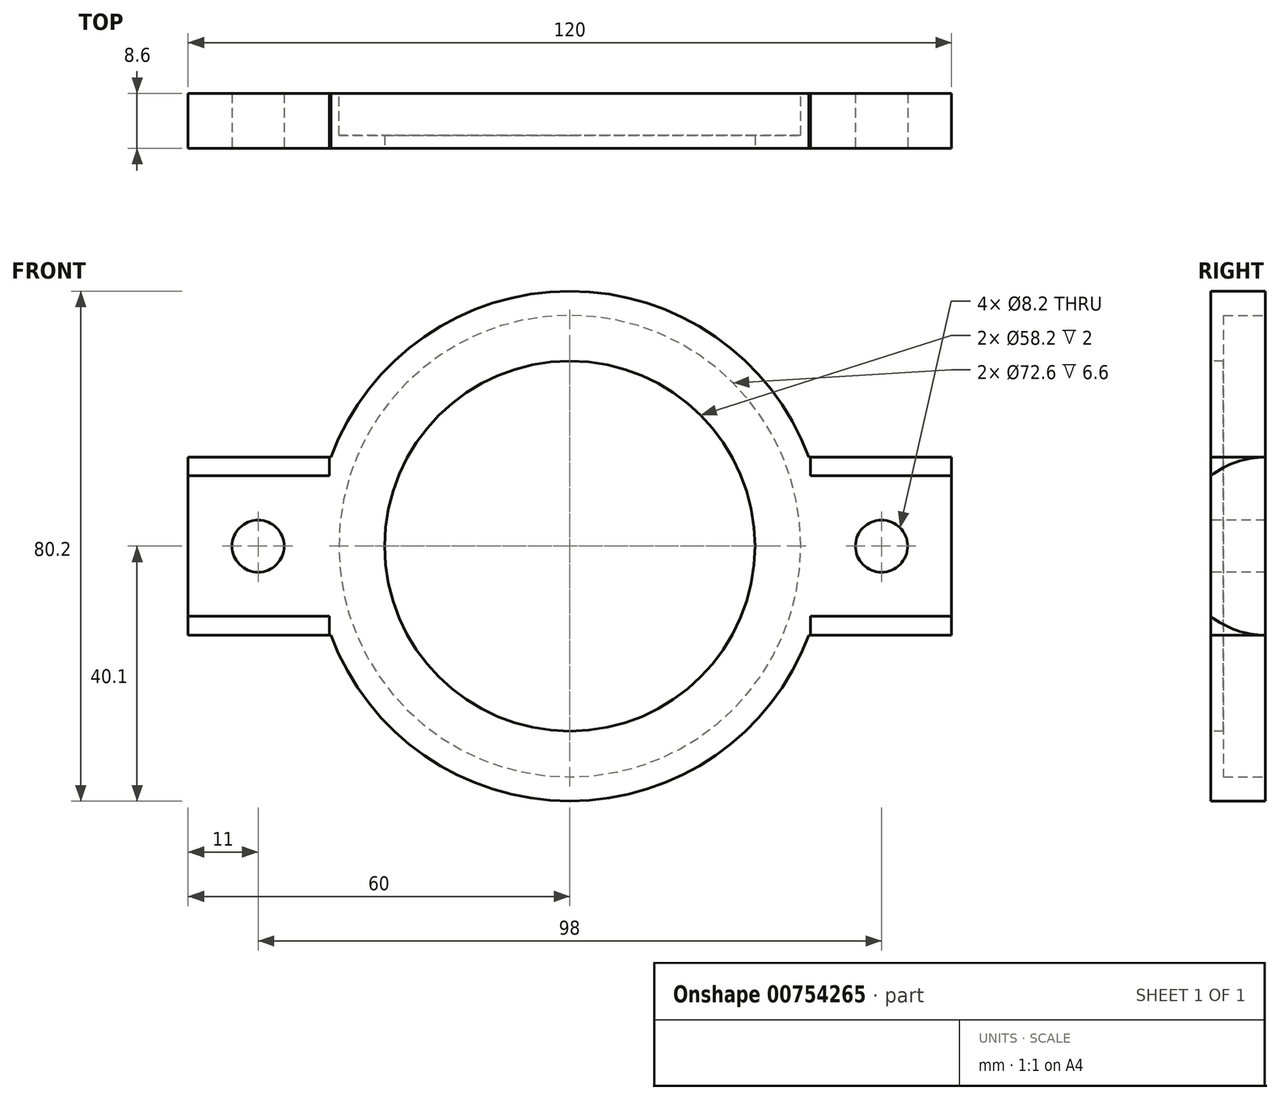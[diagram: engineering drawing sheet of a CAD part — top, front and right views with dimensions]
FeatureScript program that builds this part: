
annotation { "Feature Type Name" : "Feature", "Feature Type Description" : "" }
export const myFeature = defineFeature(function(context is Context, id is Id, definition is map)
    precondition{}
    {
        {
            var Q0;
            Q0=qCreatedBy(makeId("Front.planeOp"),FACE);
            var sketch = newSketch(context, id + "F0", { "sketchPlane" : qUnion([Q0])});
            skLineSegment(sketch, "E0.bottom", {"start": v(-60, 14) * mm, "end": v(60, 14) * mm});
            skLineSegment(sketch, "E0.top", {"start": v(-60, -14) * mm, "end": v(60, -14) * mm});
            skLineSegment(sketch, "E0.left", {"start": v(-60, 14) * mm, "end": v(-60, -14) * mm});
            skLineSegment(sketch, "E0.right", {"start": v(60, 14) * mm, "end": v(60, -14) * mm});
            skPoint(sketch, "E0.middle", {"position": v(0, 0) * mm});
            skSolve(sketch);
        }
        {
            var Q0;
            Q0=makeQuery(id+"F0.imprint","IMPRINT",FACE,{"disambiguationData":[TD([[makeQuery(id+"F0.imprint","IMPRINT",EDGE,{"derivedFrom":sQuery(id+"F0.wireOp",EDGE,"E0.bottom")}),-1.0]])]});
            extrude(context, id + "F1", {"entities" : qUnion([Q0]), "depth" : 8.6 * mm, "offsetDistance" : 25 * mm});
        }
        {
            var Q0;
            Q0=makeQuery(id+"F1.opExtrude","CAP_FACE",FACE,{"disambiguationData":[OSD([sQuery(id+"F0.wireOp",EDGE,"E0.bottom"),sQuery(id+"F0.wireOp",EDGE,"E0.top"),sQuery(id+"F0.wireOp",EDGE,"E0.left"),sQuery(id+"F0.wireOp",EDGE,"E0.right")])],"isStart":false});
            var sketch = newSketch(context, id + "F2", { "sketchPlane" : qUnion([Q0])});
            skCircle(sketch, "E1", {"center": v(0, 0) * mm, "radius": 40.1 * mm});
            skCircle(sketch, "E2", {"center": v(0, 0) * mm, "radius": 29.1 * mm});
            skSolve(sketch);
        }
        {
            var Q0;
            {var subQ0=sQuery(id+"F2.wireOp",EDGE,"E2");var subQ1=makeQuery(id+"F1.opExtrude","CAP_EDGE",EDGE,{"disambiguationData":[OSD([sQuery(id+"F0.wireOp",EDGE,"E0.bottom")])],"isStart":false});var subQ2=makeQuery(id+"F2.imprint","INTERSECT",VERTEX,{"disambiguationData":[OD(0.0)],"derivedFrom":[subQ1,subQ0]});Q0=makeQuery(id+"F2.imprint","IMPRINT",FACE,{"disambiguationData":[TD([[makeQuery(id+"F2.imprint","IMPRINT",EDGE,{"disambiguationData":[TD([[subQ2,1.0]])],"derivedFrom":subQ0}),1.0]])]});}
            var Q1;
            {var subQ0=sQuery(id+"F2.wireOp",EDGE,"E2");var subQ1=makeQuery(id+"F1.opExtrude","CAP_EDGE",EDGE,{"disambiguationData":[OSD([sQuery(id+"F0.wireOp",EDGE,"E0.bottom")])],"isStart":false});var subQ2=makeQuery(id+"F2.imprint","INTERSECT",VERTEX,{"disambiguationData":[OD(0.0)],"derivedFrom":[subQ1,subQ0]});Q1=makeQuery(id+"F2.imprint","IMPRINT",FACE,{"disambiguationData":[TD([[makeQuery(id+"F2.imprint","IMPRINT",EDGE,{"disambiguationData":[TD([[subQ2,-1.0]])],"derivedFrom":subQ0}),1.0]])]});}
            var Q2;
            {var subQ0=sQuery(id+"F2.wireOp",EDGE,"E2");var subQ1=makeQuery(id+"F1.opExtrude","CAP_EDGE",EDGE,{"disambiguationData":[OSD([sQuery(id+"F0.wireOp",EDGE,"E0.top")])],"isStart":false});var subQ2=makeQuery(id+"F2.imprint","INTERSECT",VERTEX,{"disambiguationData":[OD(0.0)],"derivedFrom":[subQ1,subQ0]});Q2=makeQuery(id+"F2.imprint","IMPRINT",FACE,{"disambiguationData":[TD([[makeQuery(id+"F2.imprint","IMPRINT",EDGE,{"disambiguationData":[TD([[subQ2,-1.0]])],"derivedFrom":subQ0}),1.0]])]});}
            extrude(context, id + "F3", {"entities" : qUnion([Q0, Q1, Q2]), "operationType" : NewBodyOperationType.REMOVE, "endBound" : BoundingType.THROUGH_ALL, "oppositeDirection" : true, "depth" : 25 * mm, "offsetDistance" : 25 * mm});
        }
        {
            var Q0;
            Q0 = qSketchRegion(id + "F2", true);
            extrude(context, id + "F4", {"entities" : qUnion([Q0]), "oppositeDirection" : true, "depth" : 8.6 * mm, "offsetDistance" : 25 * mm});
        }
        {
            var Q0;
            Q0=makeQuery(id+"F3.boolean.opBoolean","SPLIT",BODY,{"disambiguationData":[OD(0.0)],"derivedFrom":makeQuery(id+"F1.opExtrude","SWEPT_BODY",BODY,{"disambiguationData":[OSD([sQuery(id+"F0.wireOp",EDGE,"E0.bottom"),sQuery(id+"F0.wireOp",EDGE,"E0.top"),sQuery(id+"F0.wireOp",EDGE,"E0.left"),sQuery(id+"F0.wireOp",EDGE,"E0.right")])]})});
            var Q1;
            Q1=makeQuery(id+"F3.boolean.opBoolean","SPLIT",BODY,{"disambiguationData":[OD(1.0)],"derivedFrom":makeQuery(id+"F1.opExtrude","SWEPT_BODY",BODY,{"disambiguationData":[OSD([sQuery(id+"F0.wireOp",EDGE,"E0.bottom"),sQuery(id+"F0.wireOp",EDGE,"E0.top"),sQuery(id+"F0.wireOp",EDGE,"E0.left"),sQuery(id+"F0.wireOp",EDGE,"E0.right")])]})});
            var Q2;
            Q2=makeQuery(id+"F4.opExtrude","SWEPT_BODY",BODY,{"disambiguationData":[OSD([sQuery(id+"F2.wireOp",EDGE,"E1"),sQuery(id+"F2.wireOp",EDGE,"E2")])]});
            booleanBodies(context, id + "F5", {"operationType" : BooleanOperationType.UNION, "tools" : qUnion([Q0, Q1, Q2])});
        }
        {
            var Q0;
            {var subQ0=sQuery(id+"F2.wireOp",EDGE,"E2");var subQ1=sQuery(id+"F0.wireOp",EDGE,"E0.bottom");var subQ3=sQuery(id+"F0.wireOp",EDGE,"E0.right");var subQ4=sQuery(id+"F0.wireOp",EDGE,"E0.top");var subQ7=sQuery(id+"F0.wireOp",EDGE,"E0.left");var subQ8=makeQuery(id+"F1.opExtrude","CAP_FACE",FACE,{"disambiguationData":[OSD([subQ1,subQ4,subQ7,subQ3])],"isStart":false});Q0=makeQuery(id+"F5.opBoolean","MERGE",FACE,{"derivedFrom":[makeQuery(id+"F3.boolean.opBoolean","SPLIT",FACE,{"disambiguationData":[TD([makeQuery(id+"F1.opExtrude","SWEPT_FACE",FACE,{"disambiguationData":[OSD([subQ7])]})])],"derivedFrom":subQ8}),makeQuery(id+"F3.boolean.opBoolean","SPLIT",FACE,{"disambiguationData":[TD([makeQuery(id+"F1.opExtrude","SWEPT_FACE",FACE,{"disambiguationData":[OSD([subQ3])]})])],"derivedFrom":subQ8}),makeQuery(id+"F4.opExtrude","CAP_FACE",FACE,{"disambiguationData":[OSD([sQuery(id+"F2.wireOp",EDGE,"E1"),subQ0])],"isStart":true})]});}
            var sketch = newSketch(context, id + "F6", { "sketchPlane" : qUnion([Q0])});
            skCircle(sketch, "E3", {"center": v(-49, 0) * mm, "radius": 4.1 * mm});
            skCircle(sketch, "E4", {"center": v(49, 0) * mm, "radius": 4.1 * mm});
            skSolve(sketch);
        }
        {
            var Q0;
            Q0=makeQuery(id+"F6.imprint","IMPRINT",FACE,{"disambiguationData":[TD([[makeQuery(id+"F6.imprint","IMPRINT",EDGE,{"derivedFrom":sQuery(id+"F6.wireOp",EDGE,"E3")}),1.0]])]});
            var Q1;
            Q1=makeQuery(id+"F6.imprint","IMPRINT",FACE,{"disambiguationData":[TD([[makeQuery(id+"F6.imprint","IMPRINT",EDGE,{"derivedFrom":sQuery(id+"F6.wireOp",EDGE,"E4")}),1.0]])]});
            extrude(context, id + "F7", {"entities" : qUnion([Q0, Q1]), "operationType" : NewBodyOperationType.REMOVE, "endBound" : BoundingType.THROUGH_ALL, "oppositeDirection" : true, "depth" : 25 * mm, "offsetDistance" : 25 * mm});
        }
        {
            var Q0;
            Q0=makeQuery(id+"F1.opExtrude","SWEPT_FACE",FACE,{"disambiguationData":[OSD([sQuery(id+"F0.wireOp",EDGE,"E0.right")])]});
            var sketch = newSketch(context, id + "F8", { "sketchPlane" : qUnion([Q0])});
            skCircle(sketch, "E5", {"center": v(0, 0) * mm, "radius": 14 * mm});
            skSolve(sketch);
        }
        {
            var Q0;
            {var subQ1=sQuery(id+"F0.wireOp",EDGE,"E0.right");var subQ2=makeQuery(id+"F1.opExtrude","SWEPT_EDGE",EDGE,{"disambiguationData":[OSD([sQuery(id+"F0.wireOp",EDGE,"E0.bottom"),subQ1])]});Q0=makeQuery(id+"F8.imprint","IMPRINT",FACE,{"disambiguationData":[TD([[makeQuery(id+"F8.imprint","IMPRINT",EDGE,{"derivedFrom":subQ2}),-1.0]])]});}
            var Q1;
            {var subQ1=sQuery(id+"F0.wireOp",EDGE,"E0.right");var subQ2=makeQuery(id+"F1.opExtrude","SWEPT_EDGE",EDGE,{"disambiguationData":[OSD([sQuery(id+"F0.wireOp",EDGE,"E0.top"),subQ1])]});Q1=makeQuery(id+"F8.imprint","IMPRINT",FACE,{"disambiguationData":[TD([[makeQuery(id+"F8.imprint","IMPRINT",EDGE,{"derivedFrom":subQ2}),1.0]])]});}
            extrude(context, id + "F9", {"entities" : qUnion([Q0, Q1]), "operationType" : NewBodyOperationType.REMOVE, "oppositeDirection" : true, "depth" : 22.2 * mm, "offsetDistance" : 25 * mm});
        }
        {
            var Q0;
            Q0=makeQuery(id+"F1.opExtrude","SWEPT_FACE",FACE,{"disambiguationData":[OSD([sQuery(id+"F0.wireOp",EDGE,"E0.left")])]});
            var sketch = newSketch(context, id + "F10", { "sketchPlane" : qUnion([Q0])});
            skCircle(sketch, "E6", {"center": v(0, 0) * mm, "radius": 14 * mm});
            skSolve(sketch);
        }
        {
            var Q0;
            {var subQ1=sQuery(id+"F0.wireOp",EDGE,"E0.left");var subQ2=makeQuery(id+"F1.opExtrude","SWEPT_EDGE",EDGE,{"disambiguationData":[OSD([sQuery(id+"F0.wireOp",EDGE,"E0.bottom"),subQ1])]});Q0=makeQuery(id+"F10.imprint","IMPRINT",FACE,{"disambiguationData":[TD([[makeQuery(id+"F10.imprint","IMPRINT",EDGE,{"derivedFrom":subQ2}),1.0]])]});}
            var Q1;
            {var subQ1=sQuery(id+"F0.wireOp",EDGE,"E0.left");var subQ2=makeQuery(id+"F1.opExtrude","SWEPT_EDGE",EDGE,{"disambiguationData":[OSD([sQuery(id+"F0.wireOp",EDGE,"E0.top"),subQ1])]});Q1=makeQuery(id+"F10.imprint","IMPRINT",FACE,{"disambiguationData":[TD([[makeQuery(id+"F10.imprint","IMPRINT",EDGE,{"derivedFrom":subQ2}),-1.0]])]});}
            extrude(context, id + "F11", {"entities" : qUnion([Q0, Q1]), "operationType" : NewBodyOperationType.REMOVE, "oppositeDirection" : true, "depth" : 22.2 * mm, "offsetDistance" : 25 * mm});
        }
        {
            var Q0;
            {var subQ0=sQuery(id+"F2.wireOp",EDGE,"E2");var subQ1=sQuery(id+"F0.wireOp",EDGE,"E0.bottom");var subQ3=sQuery(id+"F0.wireOp",EDGE,"E0.right");var subQ4=sQuery(id+"F0.wireOp",EDGE,"E0.top");var subQ7=sQuery(id+"F0.wireOp",EDGE,"E0.left");var subQ8=makeQuery(id+"F1.opExtrude","CAP_FACE",FACE,{"disambiguationData":[OSD([subQ1,subQ4,subQ7,subQ3])],"isStart":true});Q0=makeQuery(id+"F5.opBoolean","MERGE",FACE,{"derivedFrom":[makeQuery(id+"F3.boolean.opBoolean","SPLIT",FACE,{"disambiguationData":[TD([makeQuery(id+"F1.opExtrude","SWEPT_FACE",FACE,{"disambiguationData":[OSD([subQ7])]})])],"derivedFrom":subQ8}),makeQuery(id+"F3.boolean.opBoolean","SPLIT",FACE,{"disambiguationData":[TD([makeQuery(id+"F1.opExtrude","SWEPT_FACE",FACE,{"disambiguationData":[OSD([subQ3])]})])],"derivedFrom":subQ8}),makeQuery(id+"F4.opExtrude","CAP_FACE",FACE,{"disambiguationData":[OSD([sQuery(id+"F2.wireOp",EDGE,"E1"),subQ0])],"isStart":false})]});}
            var sketch = newSketch(context, id + "F12", { "sketchPlane" : qUnion([Q0])});
            skCircle(sketch, "E7", {"center": v(0, 0) * mm, "radius": 36.3 * mm});
            skSolve(sketch);
        }
        {
            var Q0;
            Q0=makeQuery(id+"F12.imprint","IMPRINT",FACE,{"disambiguationData":[TD([[makeQuery(id+"F12.imprint","IMPRINT",EDGE,{"derivedFrom":sQuery(id+"F12.wireOp",EDGE,"E7")}),1.0]])]});
            extrude(context, id + "F13", {"entities" : qUnion([Q0]), "operationType" : NewBodyOperationType.REMOVE, "oppositeDirection" : true, "depth" : 6.6 * mm, "offsetDistance" : 25 * mm});
        }
    });
